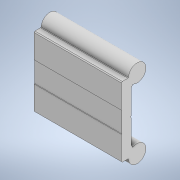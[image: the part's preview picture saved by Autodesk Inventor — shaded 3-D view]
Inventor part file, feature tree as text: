
AUTODESK INVENTOR PART (.ipt)
format: ipt  version: 2020 (Build 240168000, 168)  size: 118,784 bytes
history: native  units: mm
features: other x1, extrude x1, sketch x1
ambient origin geometry x8: Origin, YZ Plane, XZ Plane, XY Plane, X Axis, Y Axis, Z Axis, Center Point
bodies: Body1 (feature_tree)
feature tree (3):
  other  "Bryła1"
  extrude  "Wyciągnięcie proste1"  Depth=50.0mm TaperAngle=0.0deg
  sketch  "Szkic1"
